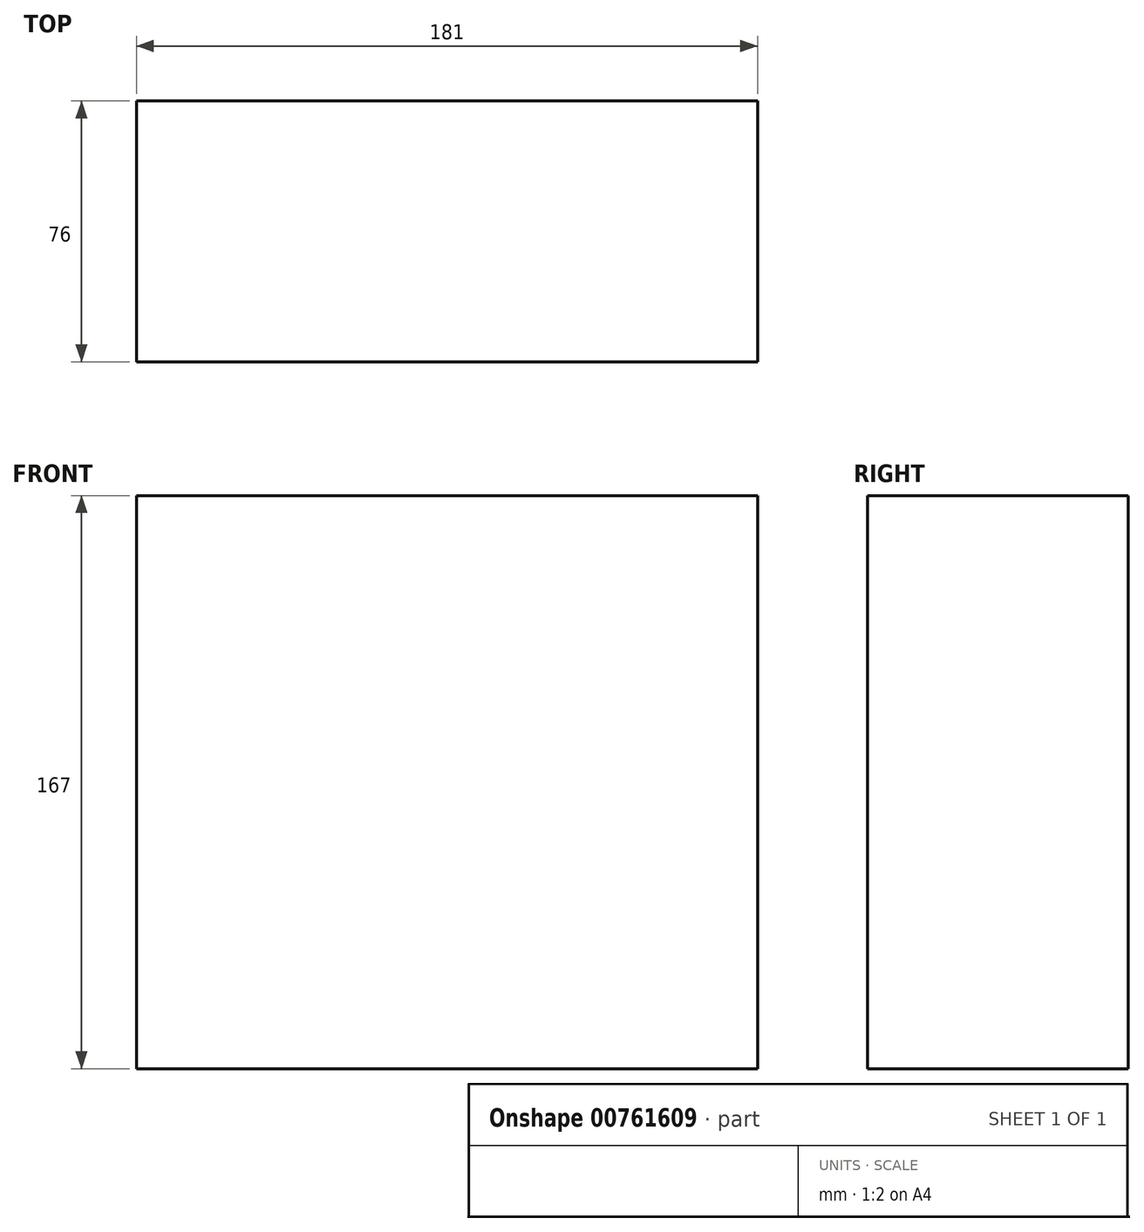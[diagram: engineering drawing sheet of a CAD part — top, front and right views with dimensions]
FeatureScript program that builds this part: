
annotation { "Feature Type Name" : "Feature", "Feature Type Description" : "" }
export const myFeature = defineFeature(function(context is Context, id is Id, definition is map)
    precondition{}
    {
        {
            var Q0;
            Q0=qCreatedBy(makeId("Top.planeOp"),FACE);
            var sketch = newSketch(context, id + "F0", { "sketchPlane" : qUnion([Q0])});
            skLineSegment(sketch, "E0.bottom", {"start": v(-181, -76) * mm, "end": v(0, -76) * mm});
            skLineSegment(sketch, "E0.top", {"start": v(-181, 0) * mm, "end": v(0, 0) * mm});
            skLineSegment(sketch, "E0.left", {"start": v(-181, -76) * mm, "end": v(-181, 0) * mm});
            skLineSegment(sketch, "E0.right", {"start": v(0, -76) * mm, "end": v(0, 0) * mm});
            skSolve(sketch);
        }
        {
            var Q0;
            Q0=makeQuery(id+"F0.imprint","IMPRINT",FACE,{"disambiguationData":[TD([[makeQuery(id+"F0.imprint","IMPRINT",EDGE,{"derivedFrom":sQuery(id+"F0.wireOp",EDGE,"E0.bottom")}),1.0]])]});
            extrude(context, id + "F1", {"entities" : qUnion([Q0]), "depth" : 167 * mm, "offsetDistance" : 25 * mm});
        }
    });
